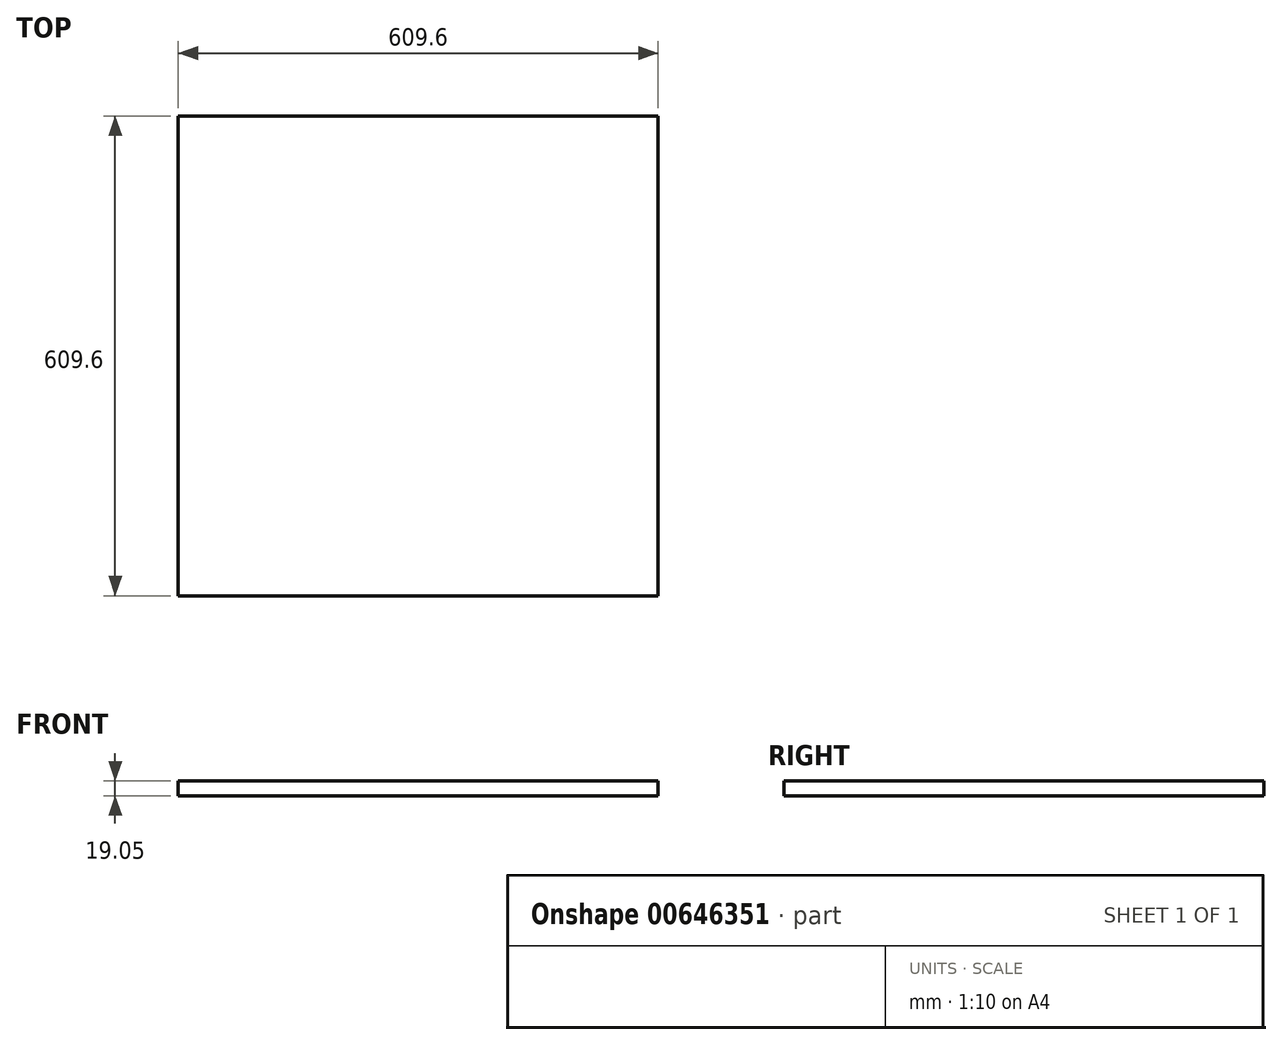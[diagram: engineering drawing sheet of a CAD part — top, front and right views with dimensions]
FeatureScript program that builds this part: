
annotation { "Feature Type Name" : "Feature", "Feature Type Description" : "" }
export const myFeature = defineFeature(function(context is Context, id is Id, definition is map)
    precondition{}
    {
        {
            var Q0;
            Q0=qCreatedBy(makeId("Top.planeOp"),FACE);
            var sketch = newSketch(context, id + "F0", { "sketchPlane" : qUnion([Q0])});
            skLineSegment(sketch, "E0.bottom", {"start": v(304.8, -304.8) * mm, "end": v(-304.8, -304.8) * mm});
            skLineSegment(sketch, "E0.top", {"start": v(304.8, 304.8) * mm, "end": v(-304.8, 304.8) * mm});
            skLineSegment(sketch, "E0.left", {"start": v(304.8, -304.8) * mm, "end": v(304.8, 304.8) * mm});
            skLineSegment(sketch, "E0.right", {"start": v(-304.8, -304.8) * mm, "end": v(-304.8, 304.8) * mm});
            skPoint(sketch, "E0.middle", {"position": v(0, 0) * mm});
            skSolve(sketch);
        }
        {
            var Q0;
            Q0=makeQuery(id+"F0.imprint","IMPRINT",FACE,{"disambiguationData":[TD([[makeQuery(id+"F0.imprint","IMPRINT",EDGE,{"derivedFrom":sQuery(id+"F0.wireOp",EDGE,"E0.bottom")}),-1.0]])]});
            extrude(context, id + "F1", {"entities" : qUnion([Q0]), "oppositeDirection" : true, "depth" : 19.05 * mm, "offsetDistance" : 25.4 * mm});
        }
    });
